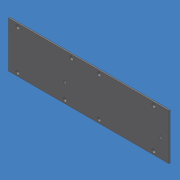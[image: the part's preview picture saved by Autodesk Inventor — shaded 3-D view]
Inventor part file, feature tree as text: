
AUTODESK INVENTOR PART (.ipt)
format: ipt  version: 2011 (Build 150239000, 239)  size: 126,464 bytes
history: native  units: mm (DEFAULTED — no unit token found)
features: sketch x4, extrude x2, hole x2
ambient origin geometry x8: Origin, YZ Plane, XZ Plane, XY Plane, X Axis, Y Axis, Z Axis, Center Point
bodies: Solid1 (feature_tree)
feature tree (8):
  extrude  "Extrusion1"  Depth=79.4258mm
  extrude  "Extrusion2"  Depth=16.3068mm
  hole  "Hole1"  [1 undecoded]
  hole  "Hole2"  [1 undecoded]
  sketch  "Sketch1"  dims[d0=277.622mm d1=79.4258mm]
  sketch  "Sketch2"  dims[d2=2.2098mm d3=0.0mm d4=16.3068mm]
  sketch  "Sketch3"  dims[d5=5.7912mm d6=5.7912mm]
  sketch  "Sketch4"  dims[d7=26.2382mm d8=120.7262mm d9=168.3004mm d10=179.7812mm d11=6.6802mm d12=4.5974mm d13=0.0mm d14=3.1496mm d15=12.7mm d16=6.731mm d17=6.35mm d18=14.3117mm d19=19.05mm d20=20.594885mm d21=47.371mm d22=14.6812mm d23=165.1mm d24=5.2324mm d25=12.7mm d26=6.731mm d27=6.35mm d28=14.3117mm d29=19.05mm d30=20.594885mm]
note: 2 required parameter values undecoded (feature->parameter linkage not recoverable at this tier; creation-order binding heuristic only, values carry confidence <= 0.55)
